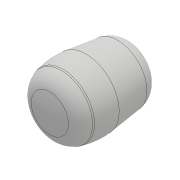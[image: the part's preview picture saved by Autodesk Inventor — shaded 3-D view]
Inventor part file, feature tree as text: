
AUTODESK INVENTOR PART (.ipt)
format: ipt  version: 2017 (Build 210142000, 142)  size: 138,752 bytes
history: native  units: mm
features: fillet x3, revolve x1, chamfer x1, thicken_offset x1, sketch x1
ambient origin geometry x8: Origin, YZ Plane, XZ Plane, XY Plane, X Axis, Y Axis, Z Axis, Center Point
bodies: Solid1 (feature_tree)
feature tree (7):
  revolve  "Revolution1"  [1 undecoded]
  fillet  "Fillet1"  Radius=30.0mm
  chamfer  "Chamfer1"  Angle=90.0deg  [1 undecoded]
  fillet  "Fillet2"  Radius=20.0mm
  fillet  "Fillet3"  Radius=10.0mm
  thicken_offset  "Thicken1"
  sketch  "Sketch1"  dims[d0=40.0mm d1=80.0mm d2=30.0mm d3=90.0deg d4=20.0mm d5=10.0mm d6=20.0mm d7=45.0deg d8=20.0mm d9=60.0mm d10=4.0mm d11=4.0mm]
note: 2 required parameter values undecoded (feature->parameter linkage not recoverable at this tier; creation-order binding heuristic only, values carry confidence <= 0.55)